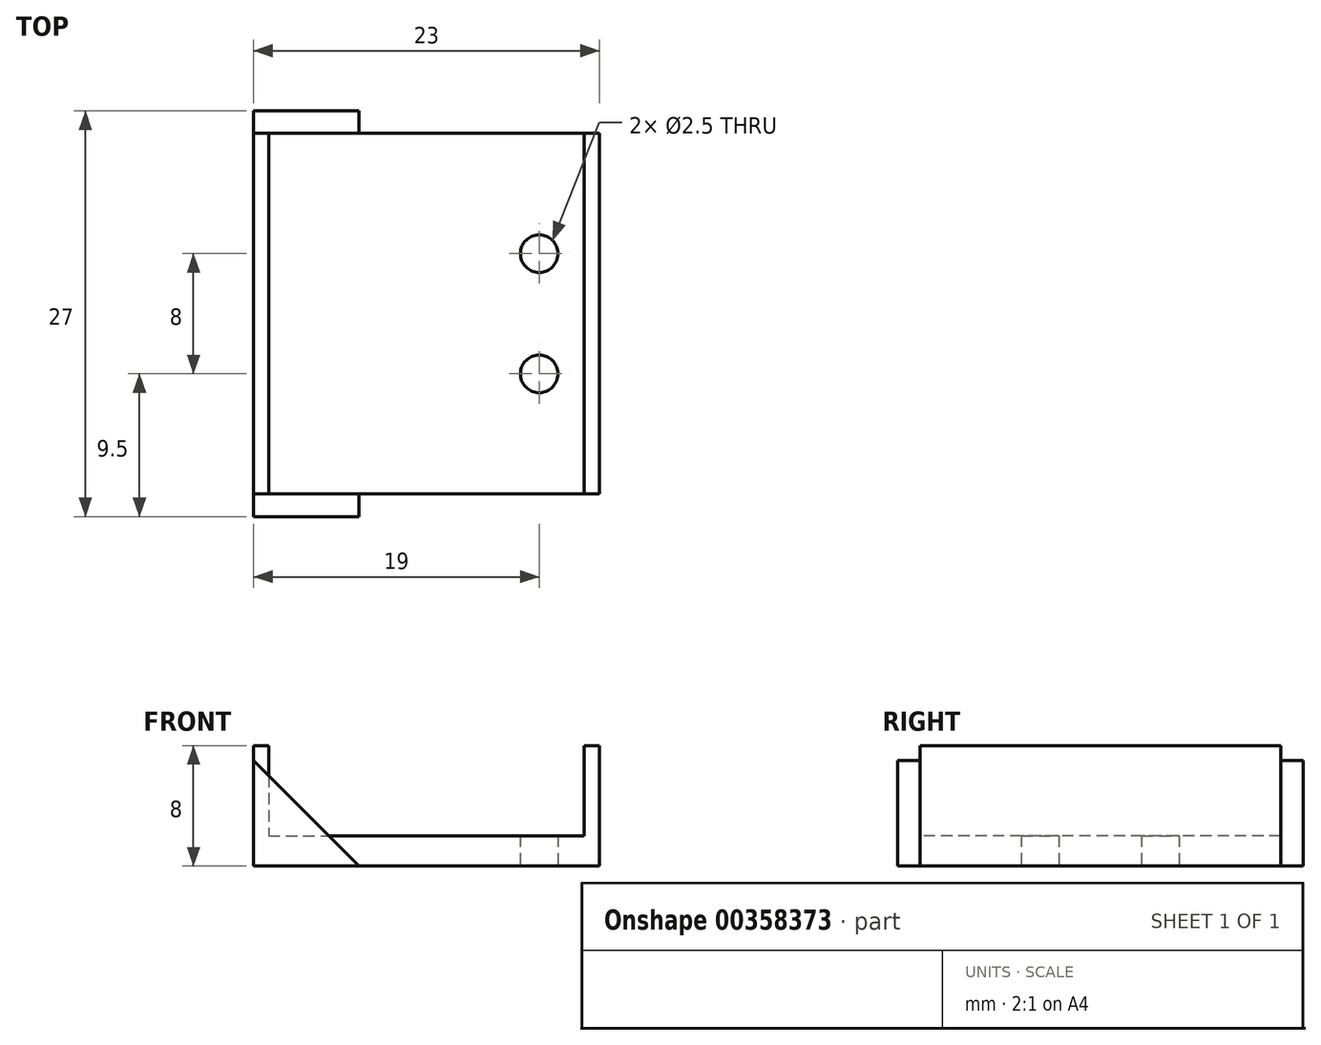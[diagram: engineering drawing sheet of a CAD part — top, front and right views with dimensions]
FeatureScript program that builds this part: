
annotation { "Feature Type Name" : "Feature", "Feature Type Description" : "" }
export const myFeature = defineFeature(function(context is Context, id is Id, definition is map)
    precondition{}
    {
        {
            var Q0;
            Q0=qCreatedBy(makeId("Top.planeOp"),FACE);
            var sketch = newSketch(context, id + "F0", { "sketchPlane" : qUnion([Q0])});
            skLineSegment(sketch, "E0.bottom", {"start": v(0, 0) * mm, "end": v(21, 0) * mm});
            skLineSegment(sketch, "E0.top", {"start": v(0, -24) * mm, "end": v(21, -24) * mm});
            skLineSegment(sketch, "E0.left", {"start": v(0, 0) * mm, "end": v(0, -24) * mm});
            skLineSegment(sketch, "E0.right", {"start": v(21, 0) * mm, "end": v(21, -24) * mm});
            skLineSegment(sketch, "E1.bottom", {"start": v(0, 0) * mm, "end": v(-1, 0) * mm});
            skLineSegment(sketch, "E1.top", {"start": v(0, -24) * mm, "end": v(-1, -24) * mm});
            skLineSegment(sketch, "E1.right", {"start": v(-1, 0) * mm, "end": v(-1, -24) * mm});
            skLineSegment(sketch, "E2.bottom", {"start": v(21, 0) * mm, "end": v(22, 0) * mm});
            skLineSegment(sketch, "E2.top", {"start": v(21, -24) * mm, "end": v(22, -24) * mm});
            skLineSegment(sketch, "E2.right", {"start": v(22, 0) * mm, "end": v(22, -24) * mm});
            skLineSegment(sketch, "E3", {"start": v(21, 0) * mm, "end": v(18, 0) * mm});
            skLineSegment(sketch, "E4", {"start": v(0, 0) * mm, "end": v(0, -8) * mm});
            skLineSegment(sketch, "E5", {"start": v(0, -8) * mm, "end": v(21, -8) * mm});
            skLineSegment(sketch, "E6", {"start": v(18, 0) * mm, "end": v(18, -24) * mm});
            skLineSegment(sketch, "E7", {"start": v(0, -24) * mm, "end": v(0, -16) * mm});
            skLineSegment(sketch, "E8", {"start": v(0, -16) * mm, "end": v(21, -16) * mm});
            skPoint(sketch, "E9", {"position": v(18, -8) * mm});
            skPoint(sketch, "E10", {"position": v(18, -16) * mm});
            skCircle(sketch, "E11", {"center": v(18, -8) * mm, "radius": 1.25 * mm});
            skCircle(sketch, "E12", {"center": v(18, -16) * mm, "radius": 1.25 * mm});
            skLineSegment(sketch, "E13", {"start": v(0, 0) * mm, "end": v(0, -12) * mm});
            skLineSegment(sketch, "E14", {"start": v(0, -12) * mm, "end": v(18, -12) * mm});
            skSolve(sketch);
        }
        {
            var Q0;
            Q0=makeQuery(id+"F0.imprint","IMPRINT",FACE,{"disambiguationData":[TD([[makeQuery(id+"F0.imprint","IMPRINT",EDGE,{"derivedFrom":sQuery(id+"F0.wireOp",EDGE,"E1.bottom")}),1.0]])]});
            var Q1;
            {var subQ3=sQuery(id+"F0.wireOp",EDGE,"E2.bottom");Q1=makeQuery(id+"F0.imprint","IMPRINT",FACE,{"disambiguationData":[TD([[makeQuery(id+"F0.imprint","IMPRINT",EDGE,{"derivedFrom":subQ3}),-1.0]])]});}
            extrude(context, id + "F1", {"entities" : qUnion([Q0, Q1]), "depth" : 8 * mm});
        }
        {
            var Q0;
            Q0 = qSketchRegion(id + "F0", true);
            var Q1;
            {var subQ1=sQuery(id+"F0.wireOp",EDGE,"E0.left");Q1=makeQuery(id+"F0.imprint","IMPRINT",FACE,{"disambiguationData":[TD([[makeQuery(id+"F0.imprint","IMPRINT",EDGE,{"derivedFrom":subQ1}),1.0]])]});}
            var Q2;
            {var subQ5=sQuery(id+"F0.wireOp",EDGE,"E5");var subQ6=sQuery(id+"F0.wireOp",EDGE,"E0.right");var subQ7=makeQuery(id+"F0.imprint","INTERSECT",VERTEX,{"derivedFrom":[subQ6,subQ5]});Q2=makeQuery(id+"F0.imprint","IMPRINT",FACE,{"disambiguationData":[TD([[makeQuery(id+"F0.imprint","IMPRINT",EDGE,{"disambiguationData":[TD([[subQ7,-1.0]])],"derivedFrom":subQ6}),-1.0]])]});}
            var Q3;
            {var subQ0=sQuery(id+"F0.wireOp",EDGE,"E14");Q3=makeQuery(id+"F0.imprint","IMPRINT",FACE,{"disambiguationData":[TD([[makeQuery(id+"F0.imprint","IMPRINT",EDGE,{"derivedFrom":subQ0}),1.0]])]});}
            extrude(context, id + "F2", {"entities" : qUnion([Q0, Q1, Q2, Q3]), "operationType" : NewBodyOperationType.ADD, "depth" : 2 * mm});
        }
        {
            var Q0;
            {var subQ0=sQuery(id+"F0.wireOp",EDGE,"E2.top");var subQ1=sQuery(id+"F0.wireOp",EDGE,"E1.top");Q0=makeQuery(id+"F2.boolean.opBoolean","MERGE",FACE,{"derivedFrom":[makeQuery(id+"F1.opExtrude","SWEPT_FACE",FACE,{"disambiguationData":[OSD([subQ1])]}),makeQuery(id+"F1.opExtrude","SWEPT_FACE",FACE,{"disambiguationData":[OSD([subQ0])]}),makeQuery(id+"F2.opExtrude","SWEPT_FACE",FACE,{"disambiguationData":[OSD([sQuery(id+"F0.wireOp",EDGE,"E0.top"),subQ1,subQ0])]})]});}
            var sketch = newSketch(context, id + "F3", { "sketchPlane" : qUnion([Q0])});
            skLineSegment(sketch, "E15", {"start": v(0, 2) * mm, "end": v(0, 6) * mm});
            skLineSegment(sketch, "E16", {"start": v(0, 2) * mm, "end": v(4, 2) * mm});
            skLineSegment(sketch, "E17", {"start": v(4, 2) * mm, "end": v(0, 6) * mm});
            skLineSegment(sketch, "E18", {"start": v(4, 2) * mm, "end": v(6, 0) * mm});
            skLineSegment(sketch, "E19", {"start": v(6, 0) * mm, "end": v(-1, 0) * mm});
            skLineSegment(sketch, "E20", {"start": v(0, 6) * mm, "end": v(-1, 7) * mm});
            skLineSegment(sketch, "E21", {"start": v(-1, 7) * mm, "end": v(-1, 0) * mm});
            skSolve(sketch);
        }
        {
            var Q0;
            Q0=makeQuery(id+"F3.imprint","IMPRINT",FACE,{"disambiguationData":[TD([[makeQuery(id+"F3.imprint","IMPRINT",EDGE,{"derivedFrom":sQuery(id+"F3.wireOp",EDGE,"E15")}),-1.0]])]});
            var Q1;
            Q1=makeQuery(id+"F3.imprint","IMPRINT",FACE,{"disambiguationData":[TD([[makeQuery(id+"F3.imprint","IMPRINT",EDGE,{"derivedFrom":sQuery(id+"F3.wireOp",EDGE,"E15")}),1.0]])]});
            extrude(context, id + "F4", {"entities" : qUnion([Q0, Q1]), "operationType" : NewBodyOperationType.ADD, "depth" : 1.5 * mm});
        }
        {
            var Q0;
            Q0=qCreatedBy(makeId("Front.planeOp"),FACE);
            cPlane(context, id + "F5", {"entities" : qUnion([Q0]), "cplaneType" : CPlaneType.OFFSET, "offset" : 12 * mm, "width" : 150 * mm, "height" : 150 * mm});
        }
        {
            var Q0;
            Q0=makeQuery(id+"F1.opExtrude","SWEPT_BODY",BODY,{"disambiguationData":[OSD([sQuery(id+"F0.wireOp",EDGE,"E1.bottom"),sQuery(id+"F0.wireOp",EDGE,"E1.top"),sQuery(id+"F0.wireOp",EDGE,"E0.left"),sQuery(id+"F0.wireOp",EDGE,"E1.right"),sQuery(id+"F0.wireOp",EDGE,"E7"),sQuery(id+"F0.wireOp",EDGE,"E13")])]});
            var Q1;
            Q1=qCreatedBy(id+"F5.planeOp",FACE);
            mirror(context, id + "F6", {"operationType" : NewBodyOperationType.ADD, "entities" : qUnion([Q0]), "mirrorPlane" : qUnion([Q1])});
        }
    });
